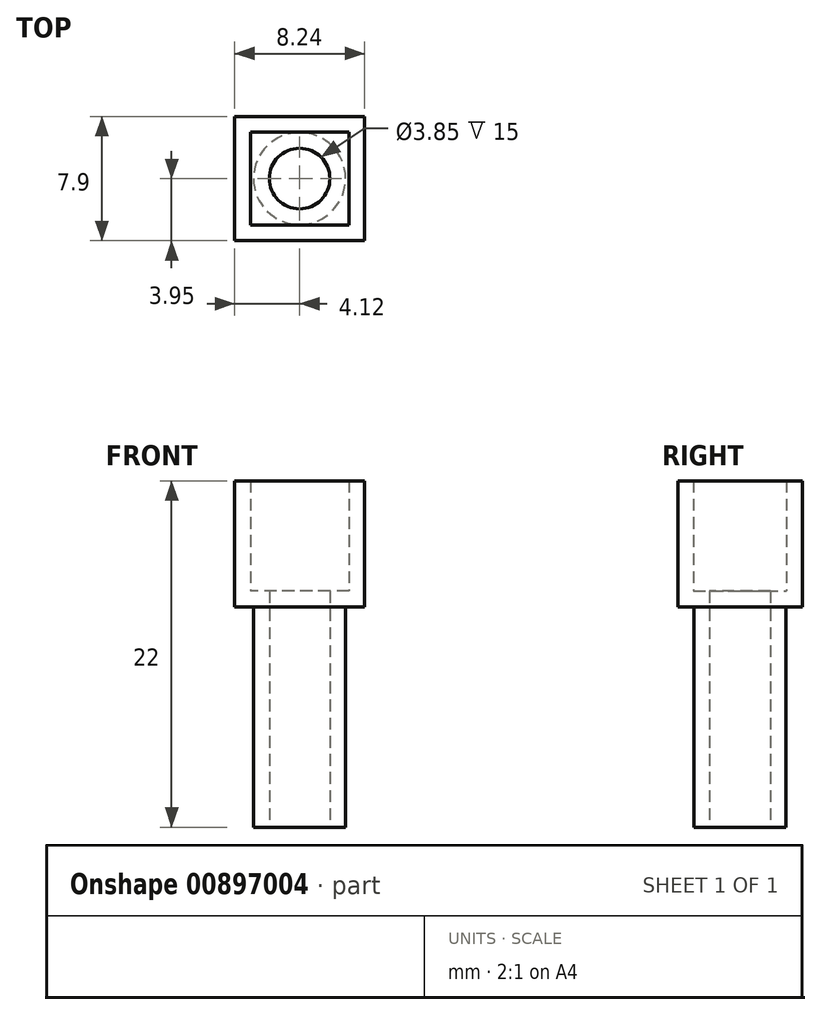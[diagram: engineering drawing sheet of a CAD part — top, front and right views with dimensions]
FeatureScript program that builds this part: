
annotation { "Feature Type Name" : "Feature", "Feature Type Description" : "" }
export const myFeature = defineFeature(function(context is Context, id is Id, definition is map)
    precondition{}
    {
        {
            var Q0;
            Q0=qCreatedBy(makeId("Top.planeOp"),FACE);
            var sketch = newSketch(context, id + "F0", { "sketchPlane" : qUnion([Q0])});
            skCircle(sketch, "E0", {"center": v(0, 0) * mm, "radius": 1.93 * mm});
            skCircle(sketch, "E1", {"center": v(0, 0) * mm, "radius": 2.93 * mm});
            skSolve(sketch);
        }
        {
            var Q0;
            Q0=makeQuery(id+"F0.imprint","IMPRINT",FACE,{"disambiguationData":[TD([[makeQuery(id+"F0.imprint","IMPRINT",EDGE,{"derivedFrom":sQuery(id+"F0.wireOp",EDGE,"E0")}),-1.0]])]});
            extrude(context, id + "F1", {"entities" : qUnion([Q0]), "depth" : 15 * mm, "offsetDistance" : 25 * mm});
        }
        {
            var Q0;
            Q0=makeQuery(id+"F1.opExtrude","CAP_FACE",FACE,{"disambiguationData":[OSD([sQuery(id+"F0.wireOp",EDGE,"E0"),sQuery(id+"F0.wireOp",EDGE,"E1")])],"isStart":false});
            var sketch = newSketch(context, id + "F2", { "sketchPlane" : qUnion([Q0])});
            skSolve(sketch);
        }
        {
            var Q0;
            Q0=makeQuery(id+"F2.imprint","IMPRINT",FACE,{"disambiguationData":[TD([[makeQuery(id+"F2.imprint","IMPRINT",EDGE,{"derivedFrom":makeQuery(id+"F1.opExtrude","CAP_EDGE",EDGE,{"disambiguationData":[OSD([sQuery(id+"F0.wireOp",EDGE,"E0")])],"isStart":false})}),-1.0]])]});
            var sketch = newSketch(context, id + "F3", { "sketchPlane" : qUnion([Q0])});
            skLineSegment(sketch, "E2.bottom", {"start": v(3.13, -2.95) * mm, "end": v(-3.12, -2.95) * mm});
            skLineSegment(sketch, "E2.top", {"start": v(3.12, 2.95) * mm, "end": v(-3.13, 2.95) * mm});
            skLineSegment(sketch, "E2.left", {"start": v(3.13, -2.95) * mm, "end": v(3.12, 2.95) * mm});
            skLineSegment(sketch, "E2.right", {"start": v(-3.12, -2.95) * mm, "end": v(-3.12, 2.95) * mm});
            skPoint(sketch, "E2.middle", {"position": v(0, 0) * mm});
            skLineSegment(sketch, "E3.bottom", {"start": v(4.13, 3.95) * mm, "end": v(-4.12, 3.95) * mm});
            skLineSegment(sketch, "E3.top", {"start": v(4.13, -3.95) * mm, "end": v(-4.12, -3.95) * mm});
            skLineSegment(sketch, "E3.left", {"start": v(4.13, 3.95) * mm, "end": v(4.13, -3.95) * mm});
            skLineSegment(sketch, "E3.right", {"start": v(-4.12, 3.95) * mm, "end": v(-4.12, -3.95) * mm});
            skSolve(sketch);
        }
        {
            var Q0;
            Q0 = qSketchRegion(id + "F3", true);
            var Q1;
            Q1=makeQuery(id+"F3.imprint","IMPRINT",FACE,{"disambiguationData":[TD([[makeQuery(id+"F3.imprint","IMPRINT",EDGE,{"derivedFrom":sQuery(id+"F3.wireOp",EDGE,"E2.bottom")}),1.0]])]});
            var Q2;
            Q2=makeQuery(id+"F3.imprint","IMPRINT",FACE,{"disambiguationData":[TD([[makeQuery(id+"F3.imprint","IMPRINT",EDGE,{"derivedFrom":sQuery(id+"F3.wireOp",EDGE,"E2.bottom")}),-1.0]])]});
            extrude(context, id + "F4", {"entities" : qUnion([Q0, Q1, Q2]), "operationType" : NewBodyOperationType.ADD, "oppositeDirection" : true, "depth" : 1 * mm, "offsetDistance" : 25 * mm});
        }
        {
            var Q0;
            Q0=makeQuery(id+"F3.imprint","IMPRINT",FACE,{"disambiguationData":[TD([[makeQuery(id+"F3.imprint","IMPRINT",EDGE,{"derivedFrom":sQuery(id+"F3.wireOp",EDGE,"E2.bottom")}),1.0]])]});
            extrude(context, id + "F5", {"entities" : qUnion([Q0]), "operationType" : NewBodyOperationType.ADD, "depth" : 7 * mm, "offsetDistance" : 25 * mm});
        }
    });
